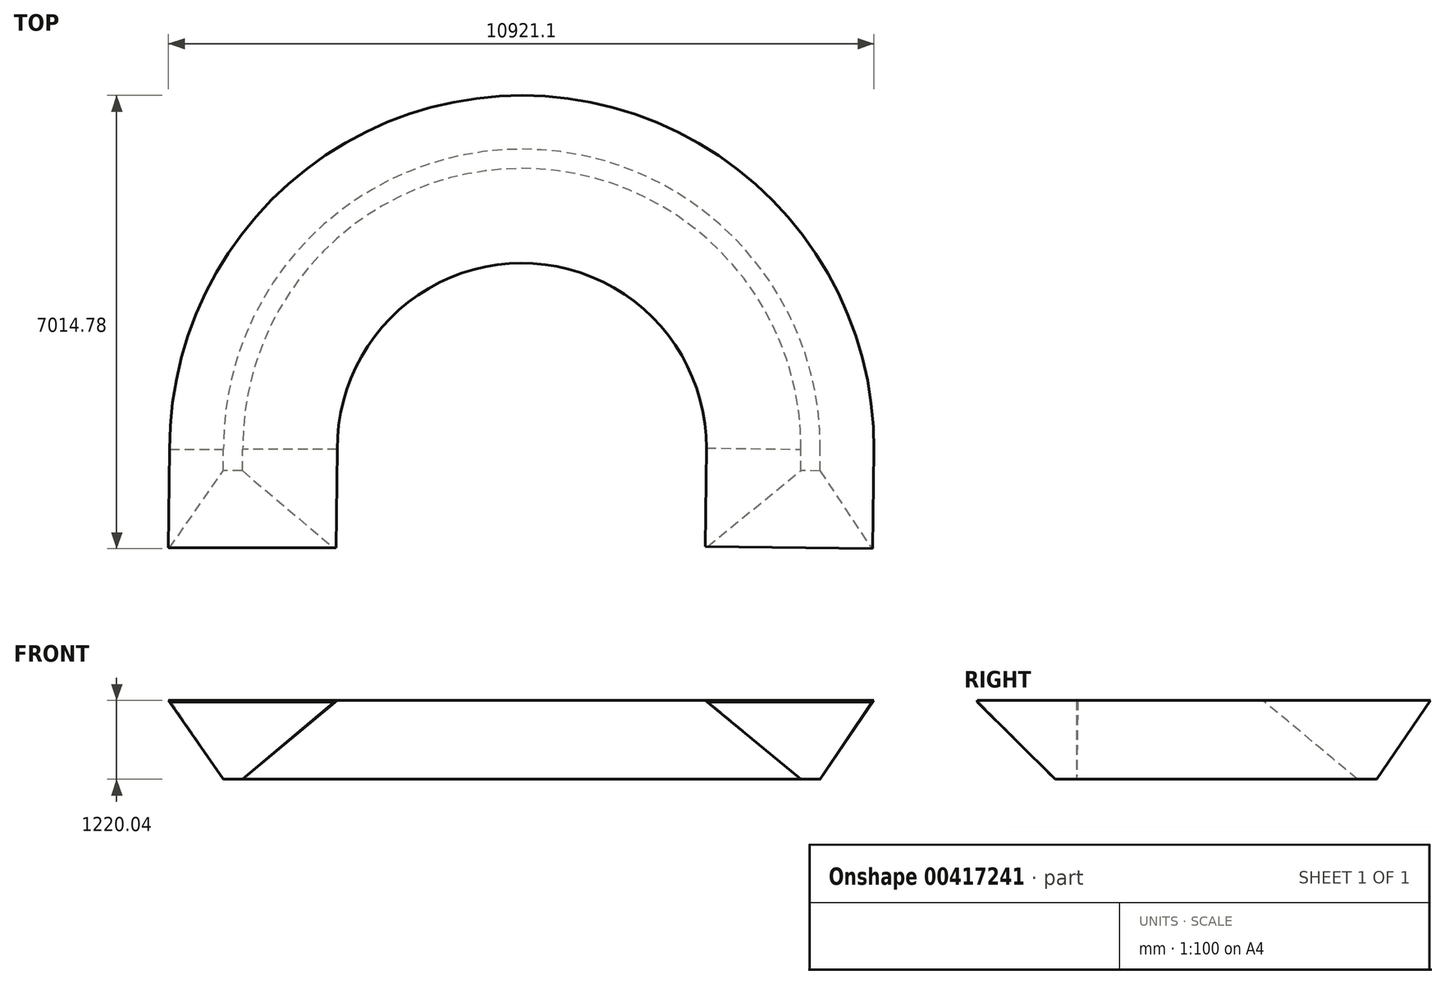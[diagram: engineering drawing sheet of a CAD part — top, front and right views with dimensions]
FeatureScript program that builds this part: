
annotation { "Feature Type Name" : "Feature", "Feature Type Description" : "" }
export const myFeature = defineFeature(function(context is Context, id is Id, definition is map)
    precondition{}
    {
        {
            var Q0;
            Q0=qCreatedBy(makeId("Top.planeOp"),FACE);
            var sketch = newSketch(context, id + "F0", { "sketchPlane" : qUnion([Q0])});
            skArc(sketch, "E0", {"start": v(9143.82, 0) * mm, "mid": v(4571.9, 4600.82) * mm, "end": v(0, 0) * mm});
            skSolve(sketch);
        }
        {
            var Q0;
            Q0=qCreatedBy(makeId("Front.planeOp"),FACE);
            var sketch = newSketch(context, id + "F1", { "sketchPlane" : qUnion([Q0])});
            skLineSegment(sketch, "E1", {"start": v(0, 0) * mm, "end": v(-879.01, 0) * mm});
            skLineSegment(sketch, "E2", {"start": v(0, 0) * mm, "end": v(1715.57, 0) * mm});
            skLineSegment(sketch, "E3", {"start": v(-879.01, 0) * mm, "end": v(-47.99, -1219.05) * mm});
            skLineSegment(sketch, "E4", {"start": v(1715.57, 0) * mm, "end": v(250.47, -1220.04) * mm});
            skLineSegment(sketch, "E5", {"start": v(250.47, -1220.04) * mm, "end": v(-47.99, -1219.05) * mm});
            skSolve(sketch);
        }
        {
            var Q0;
            Q0=makeQuery(id+"F1.imprint","IMPRINT",FACE,{"disambiguationData":[TD([[makeQuery(id+"F1.imprint","IMPRINT",EDGE,{"derivedFrom":sQuery(id+"F1.wireOp",EDGE,"E1")}),1.0]])]});
            var Q1;
            Q1=sQuery(id+"F0.wireOp",EDGE,"E0");
            sweep(context, id + "F2", {"profiles" : qUnion([Q0]), "path" : qUnion([Q1])});
        }
        {
            var Q0;
            Q0=makeQuery(id+"F2.opSweep","CAP_FACE",FACE,{"disambiguationData":[OSD([sQuery(id+"F0.wireOp",VERTEX,"E0.start"),sQuery(id+"F1.wireOp",EDGE,"E1"),sQuery(id+"F1.wireOp",EDGE,"E2"),sQuery(id+"F1.wireOp",EDGE,"E3"),sQuery(id+"F1.wireOp",EDGE,"E4"),sQuery(id+"F1.wireOp",EDGE,"E5")])],"isStart":false});
            var Q1;
            Q1=makeQuery(id+"F2.opSweep","CAP_FACE",FACE,{"disambiguationData":[OSD([sQuery(id+"F0.wireOp",VERTEX,"E0.end"),sQuery(id+"F1.wireOp",EDGE,"E1"),sQuery(id+"F1.wireOp",EDGE,"E2"),sQuery(id+"F1.wireOp",EDGE,"E3"),sQuery(id+"F1.wireOp",EDGE,"E4"),sQuery(id+"F1.wireOp",EDGE,"E5")])],"isStart":true});
            extrude(context, id + "F3", {"entities" : qUnion([Q0, Q1]), "operationType" : NewBodyOperationType.ADD, "depth" : 1524 * mm});
        }
        {
            var Q0;
            Q0=makeQuery(id+"F3.opExtrude","CAP_EDGE",EDGE,{"disambiguationData":[OSD([sQuery(id+"F0.wireOp",VERTEX,"E0.start"),sQuery(id+"F1.wireOp",EDGE,"E5")])],"isStart":false});
            chamfer(context, id + "F4", {"entities" : qUnion([Q0]), "width" : 1193.8 * mm, "tangentPropagation" : true});
        }
        {
            var Q0;
            Q0=makeQuery(id+"F3.opExtrude","CAP_EDGE",EDGE,{"disambiguationData":[OSD([sQuery(id+"F0.wireOp",VERTEX,"E0.end"),sQuery(id+"F1.wireOp",EDGE,"E5")]),OD(0.0)],"isStart":false});
            chamfer(context, id + "F5", {"entities" : qUnion([Q0]), "width" : 1193.8 * mm, "tangentPropagation" : true});
        }
    });
